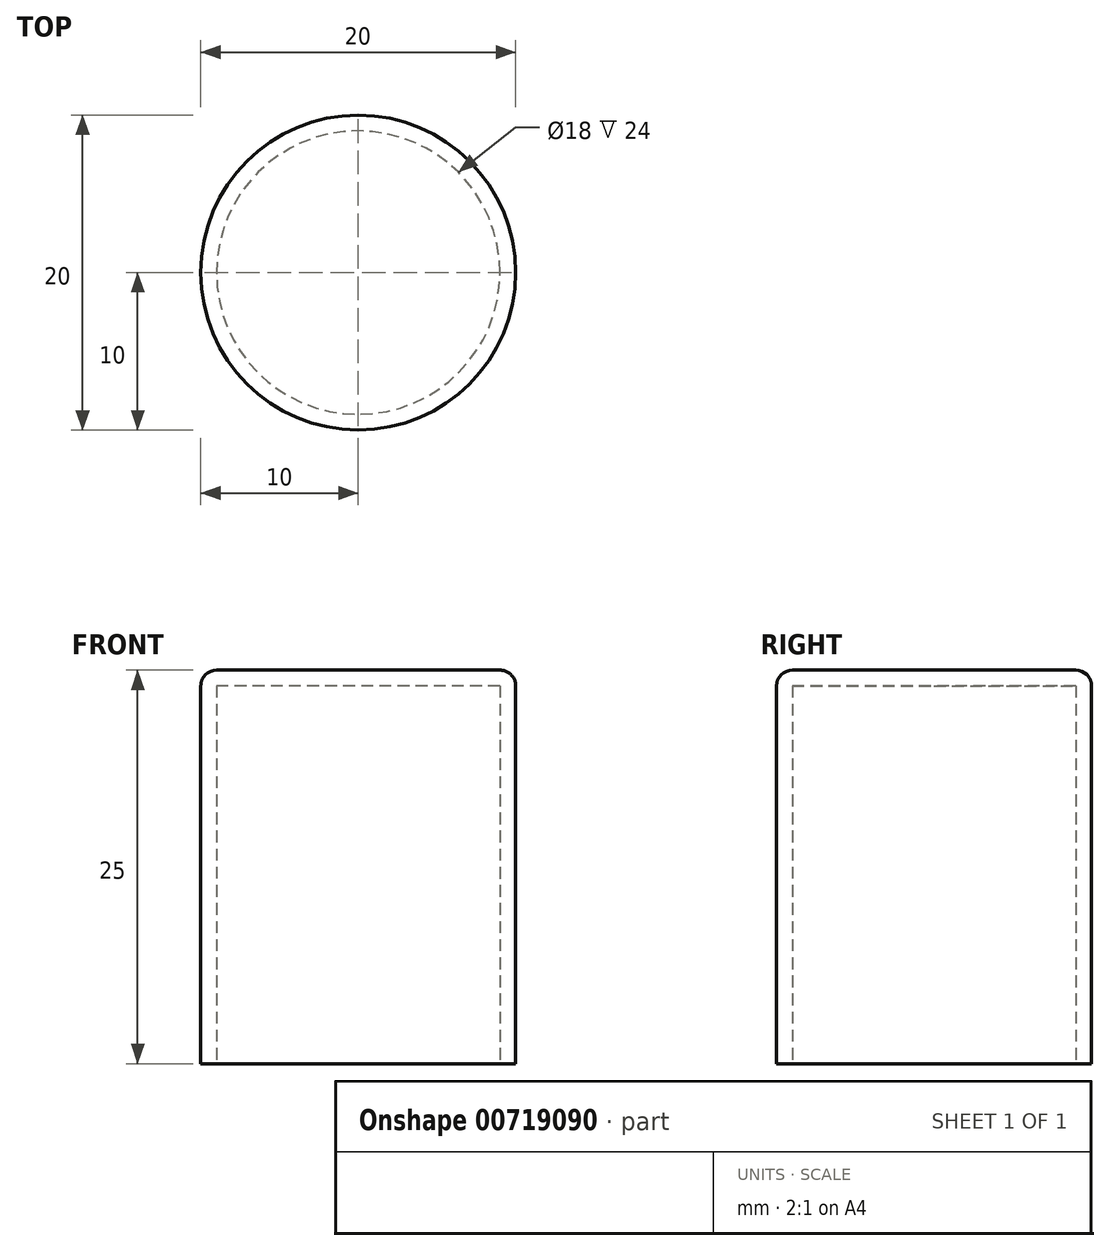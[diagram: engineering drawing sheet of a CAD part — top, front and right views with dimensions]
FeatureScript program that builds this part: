
annotation { "Feature Type Name" : "Feature", "Feature Type Description" : "" }
export const myFeature = defineFeature(function(context is Context, id is Id, definition is map)
    precondition{}
    {
        {
            var Q0;
            Q0=qCreatedBy(makeId("Top.planeOp"),FACE);
            var sketch = newSketch(context, id + "F0", { "sketchPlane" : qUnion([Q0])});
            skCircle(sketch, "E0", {"center": v(0, 0) * mm, "radius": 10 * mm});
            skSolve(sketch);
        }
        {
            var Q0;
            Q0=makeQuery(id+"F0.imprint","IMPRINT",FACE,{"disambiguationData":[TD([[makeQuery(id+"F0.imprint","IMPRINT",EDGE,{"derivedFrom":sQuery(id+"F0.wireOp",EDGE,"E0")}),1.0]])]});
            extrude(context, id + "F1", {"entities" : qUnion([Q0]), "depth" : 25 * mm, "offsetDistance" : 25 * mm});
        }
        {
            var Q0;
            Q0=makeQuery(id+"F1.opExtrude","CAP_FACE",FACE,{"disambiguationData":[OSD([sQuery(id+"F0.wireOp",EDGE,"E0")])],"isStart":true});
            shell(context, id + "F2", {"entities" : qUnion([Q0]), "thickness" : 1 * mm});
        }
        {
            var Q0;
            Q0=makeQuery(id+"F1.opExtrude","CAP_EDGE",EDGE,{"disambiguationData":[OSD([sQuery(id+"F0.wireOp",EDGE,"E0")])],"isStart":false});
            fillet(context, id + "F3", {"entities" : qUnion([Q0]), "radius" : 1 * mm, "tangentPropagation" : true, "allowEdgeOverflow" : false});
        }
    });
